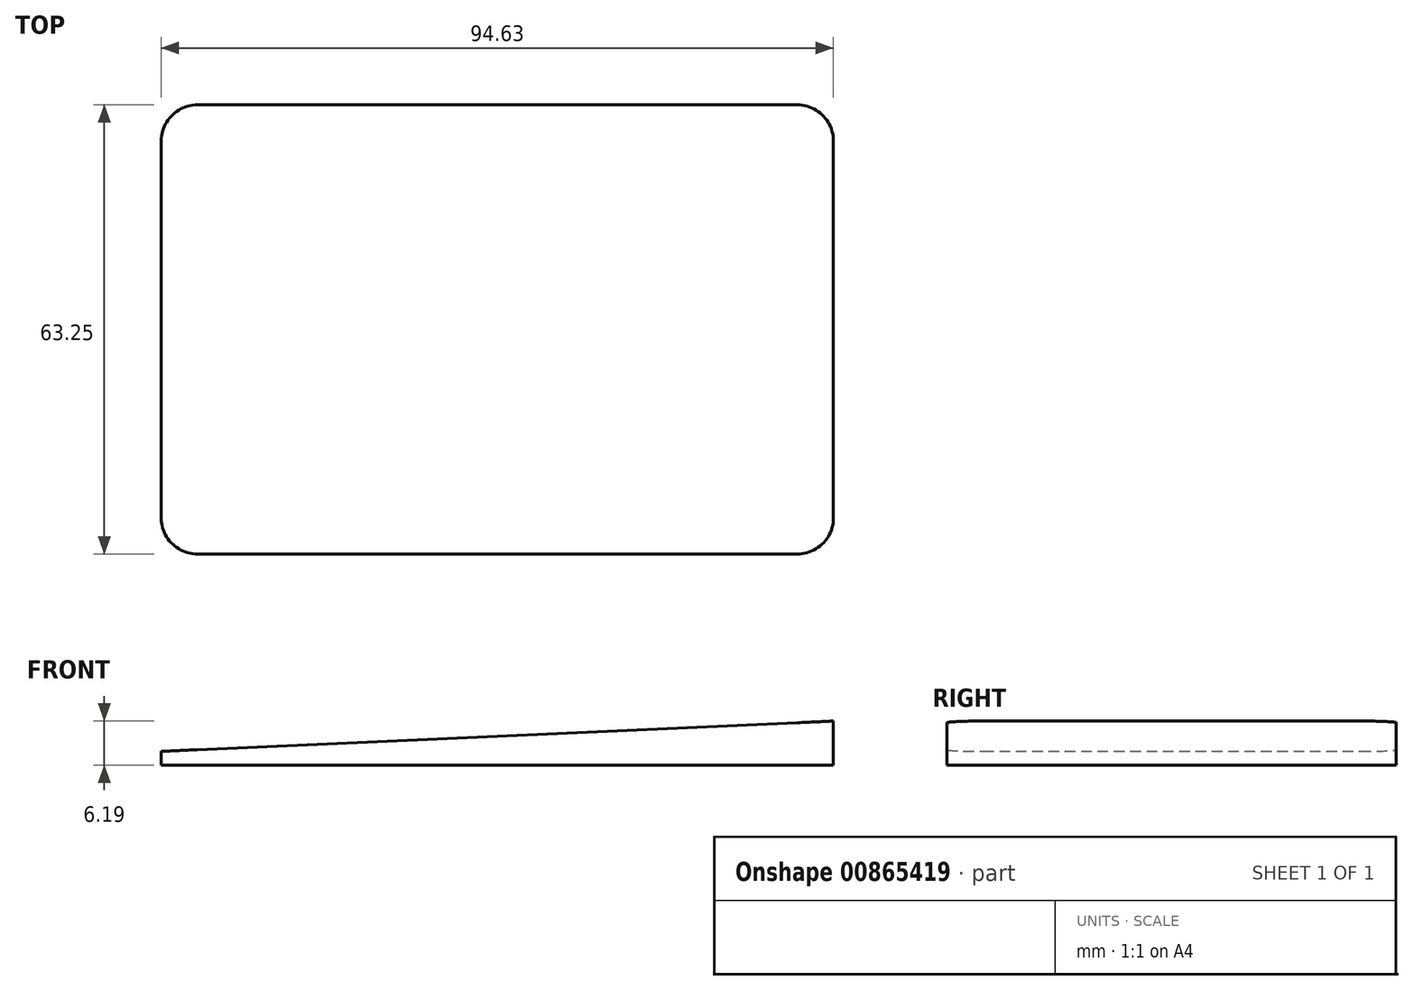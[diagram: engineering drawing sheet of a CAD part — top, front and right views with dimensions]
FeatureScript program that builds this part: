
annotation { "Feature Type Name" : "Feature", "Feature Type Description" : "" }
export const myFeature = defineFeature(function(context is Context, id is Id, definition is map)
    precondition{}
    {
        {
            var Q0;
            Q0=qCreatedBy(makeId("Front.planeOp"),FACE);
            var sketch = newSketch(context, id + "F0", { "sketchPlane" : qUnion([Q0])});
            skLineSegment(sketch, "E0", {"start": v(-46.4, 0) * mm, "end": v(48.23, 0) * mm});
            skLineSegment(sketch, "E1", {"start": v(48.23, 0) * mm, "end": v(48.23, 6.2) * mm});
            skLineSegment(sketch, "E2", {"start": v(48.23, 6.2) * mm, "end": v(-46.4, 1.93) * mm});
            skLineSegment(sketch, "E3", {"start": v(-46.4, 1.93) * mm, "end": v(-46.4, 0) * mm});
            skSolve(sketch);
        }
        {
            var Q0;
            Q0=makeQuery(id+"F0.imprint","IMPRINT",FACE,{"disambiguationData":[TD([[makeQuery(id+"F0.imprint","IMPRINT",EDGE,{"derivedFrom":sQuery(id+"F0.wireOp",EDGE,"E0")}),1.0]])]});
            extrude(context, id + "F1", {"entities" : qUnion([Q0]), "depth" : 63.25 * mm, "offsetDistance" : 25.4 * mm});
        }
        {
            var Q0;
            Q0=makeQuery(id+"F1.opExtrude","CAP_EDGE",EDGE,{"disambiguationData":[OSD([sQuery(id+"F0.wireOp",EDGE,"E1")])],"isStart":true});
            var Q1;
            Q1=makeQuery(id+"F1.opExtrude","CAP_EDGE",EDGE,{"disambiguationData":[OSD([sQuery(id+"F0.wireOp",EDGE,"E1")])],"isStart":false});
            var Q2;
            Q2=makeQuery(id+"F1.opExtrude","CAP_EDGE",EDGE,{"disambiguationData":[OSD([sQuery(id+"F0.wireOp",EDGE,"E3")])],"isStart":false});
            var Q3;
            Q3=makeQuery(id+"F1.opExtrude","CAP_EDGE",EDGE,{"disambiguationData":[OSD([sQuery(id+"F0.wireOp",EDGE,"E3")])],"isStart":true});
            fillet(context, id + "F2", {"entities" : qUnion([Q0, Q1, Q2, Q3]), "radius" : 5.08 * mm, "tangentPropagation" : true, "allowEdgeOverflow" : false});
        }
        {
            var Q0;
            Q0=makeQuery(id+"F1.opExtrude","SWEPT_FACE",FACE,{"disambiguationData":[OSD([sQuery(id+"F0.wireOp",EDGE,"E2")])]});
            var sketch = newSketch(context, id + "F3", { "sketchPlane" : qUnion([Q0])});
            skLineSegment(sketch, "E4.bottom", {"start": v(38.29, -5.08) * mm, "end": v(-4.19, -5.08) * mm});
            skLineSegment(sketch, "E4.top", {"start": v(38.29, -58.7) * mm, "end": v(-4.19, -58.7) * mm});
            skLineSegment(sketch, "E4.left", {"start": v(38.29, -5.08) * mm, "end": v(38.29, -58.7) * mm});
            skLineSegment(sketch, "E4.right", {"start": v(-4.19, -5.08) * mm, "end": v(-4.19, -58.7) * mm});
            skSolve(sketch);
        }
        {
            var Q0;
            Q0=makeQuery(id+"F3.imprint","IMPRINT",FACE,{"disambiguationData":[TD([[makeQuery(id+"F3.imprint","IMPRINT",EDGE,{"derivedFrom":sQuery(id+"F3.wireOp",EDGE,"E4.bottom")}),1.0]])]});
            extrude(context, id + "F4", {"entities" : qUnion([Q0]), "operationType" : NewBodyOperationType.ADD, "oppositeDirection" : true, "depth" : 1.27 * mm, "offsetDistance" : 25.4 * mm});
        }
    });
